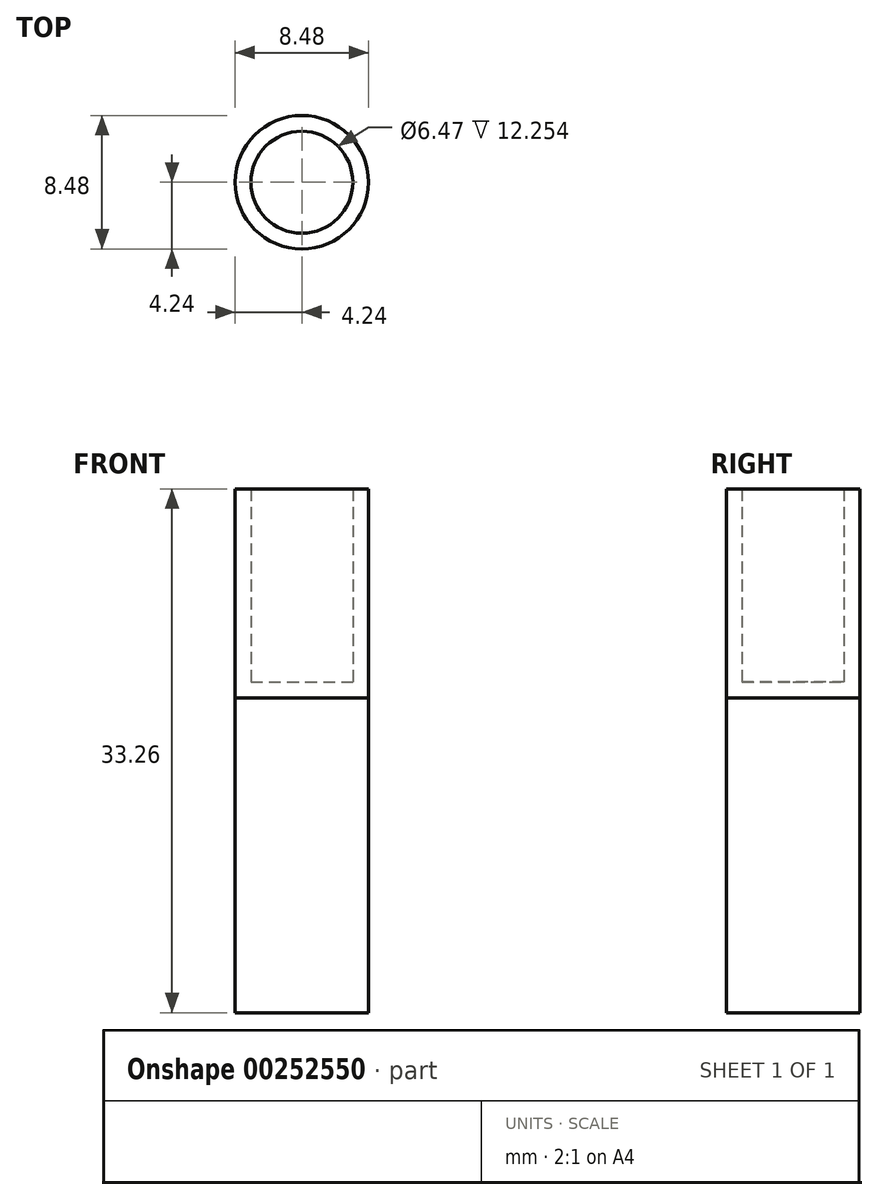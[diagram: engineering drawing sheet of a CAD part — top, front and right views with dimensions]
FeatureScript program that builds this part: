
annotation { "Feature Type Name" : "Feature", "Feature Type Description" : "" }
export const myFeature = defineFeature(function(context is Context, id is Id, definition is map)
    precondition{}
    {
        {
            var Q0;
            Q0=qCreatedBy(makeId("Front.planeOp"),FACE);
            var sketch = newSketch(context, id + "F0", { "sketchPlane" : qUnion([Q0])});
            skLineSegment(sketch, "E0.bottom", {"start": v(-3.76, -6.63) * mm, "end": v(4.24, -6.63) * mm});
            skLineSegment(sketch, "E0.top", {"start": v(-3.76, 6.63) * mm, "end": v(4.24, 6.63) * mm});
            skLineSegment(sketch, "E0.left", {"start": v(-3.76, -6.63) * mm, "end": v(-3.76, 6.63) * mm});
            skLineSegment(sketch, "E0.right", {"start": v(4.24, -6.63) * mm, "end": v(4.24, 6.63) * mm});
            skPoint(sketch, "E0.middle", {"position": v(0.24, 0) * mm});
            skLineSegment(sketch, "E1", {"start": v(0, 6.63) * mm, "end": v(0, -6.63) * mm});
            skLineSegment(sketch, "E2", {"start": v(0, -6.63) * mm, "end": v(0, 6.63) * mm});
            skSolve(sketch);
        }
        {
            var Q0;
            {var subQ0=sQuery(id+"F0.wireOp",EDGE,"E0.right");Q0=makeQuery(id+"F0.imprint","IMPRINT",FACE,{"disambiguationData":[TD([[makeQuery(id+"F0.imprint","IMPRINT",EDGE,{"derivedFrom":subQ0}),1.0]])]});}
            var Q1;
            Q1=sQuery(id+"F0.wireOp",EDGE,"E2");
            revolve(context, id + "F1", {"entities" : qUnion([Q0]), "axis" : qUnion([Q1]), "revolveType" : RevolveType.FULL});
        }
        {
            var Q0;
            Q0=makeQuery(id+"F1.opRevolve","SWEPT_FACE",FACE,{"disambiguationData":[OSD([sQuery(id+"F0.wireOp",EDGE,"E0.top")])]});
            shell(context, id + "F2", {"entities" : qUnion([Q0]), "thickness" : 1 * mm});
        }
        {
            var Q0;
            Q0=makeQuery(id+"F1.opRevolve","SWEPT_FACE",FACE,{"disambiguationData":[OSD([sQuery(id+"F0.wireOp",EDGE,"E0.bottom")])]});
            extrude(context, id + "F3", {"entities" : qUnion([Q0]), "depth" : 20 * mm});
        }
    });
